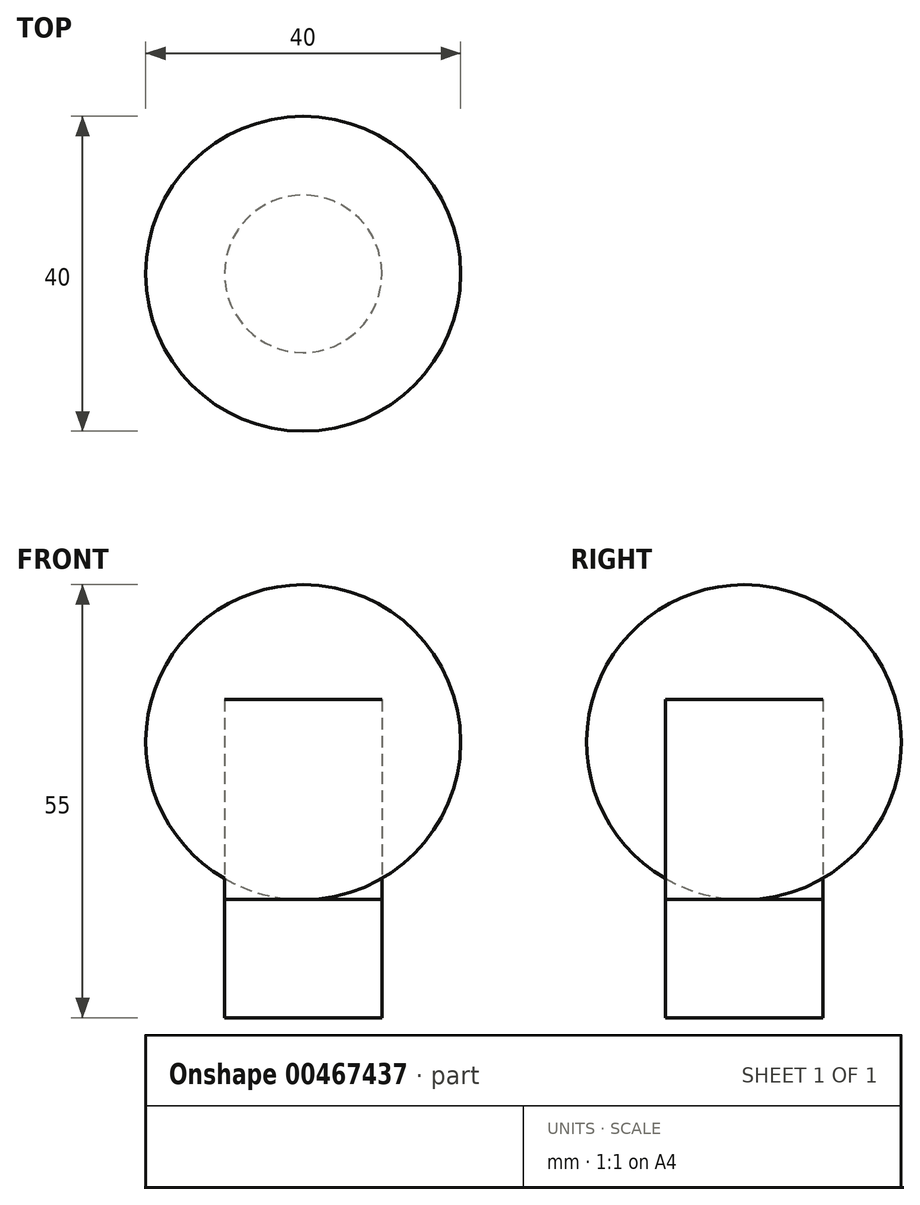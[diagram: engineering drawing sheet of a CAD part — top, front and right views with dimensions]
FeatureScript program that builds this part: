
annotation { "Feature Type Name" : "Feature", "Feature Type Description" : "" }
export const myFeature = defineFeature(function(context is Context, id is Id, definition is map)
    precondition{}
    {
        {
            var Q0;
            Q0=qCreatedBy(makeId("Front.planeOp"),FACE);
            var sketch = newSketch(context, id + "F0", { "sketchPlane" : qUnion([Q0])});
            skArc(sketch, "E0", {"start": v(0, -20) * mm, "mid": v(20, 0) * mm, "end": v(0, 20) * mm});
            skLineSegment(sketch, "E1", {"start": v(0, 20) * mm, "end": v(0, -20) * mm});
            skLineSegment(sketch, "E2.bottom", {"start": v(0, -20) * mm, "end": v(10, -20) * mm});
            skLineSegment(sketch, "E2.top", {"start": v(0, -35) * mm, "end": v(10, -35) * mm});
            skLineSegment(sketch, "E2.left", {"start": v(0, -20) * mm, "end": v(0, -35) * mm});
            skLineSegment(sketch, "E2.right", {"start": v(10, -20) * mm, "end": v(10, -35) * mm});
            skSolve(sketch);
        }
        {
            var Q0;
            Q0=makeQuery(id+"F0.imprint","IMPRINT",FACE,{"disambiguationData":[TD([[makeQuery(id+"F0.imprint","IMPRINT",EDGE,{"derivedFrom":sQuery(id+"F0.wireOp",EDGE,"E0")}),1.0]])]});
            var Q1;
            Q1=makeQuery(id+"F0.imprint","IMPRINT",FACE,{"disambiguationData":[TD([[makeQuery(id+"F0.imprint","IMPRINT",EDGE,{"derivedFrom":sQuery(id+"F0.wireOp",EDGE,"E2.bottom")}),-1.0]])]});
            var Q2;
            Q2=sQuery(id+"F0.wireOp",EDGE,"E1");
            revolve(context, id + "F1", {"entities" : qUnion([Q0, Q1]), "axis" : qUnion([Q2]), "revolveType" : RevolveType.FULL});
        }
        {
            var Q0;
            Q0=makeQuery(id+"F1.opRevolve","SWEPT_FACE",FACE,{"disambiguationData":[OSD([sQuery(id+"F0.wireOp",EDGE,"E2.bottom")])]});
            extrude(context, id + "F2", {"entities" : qUnion([Q0]), "depth" : 25.4 * mm});
        }
    });
